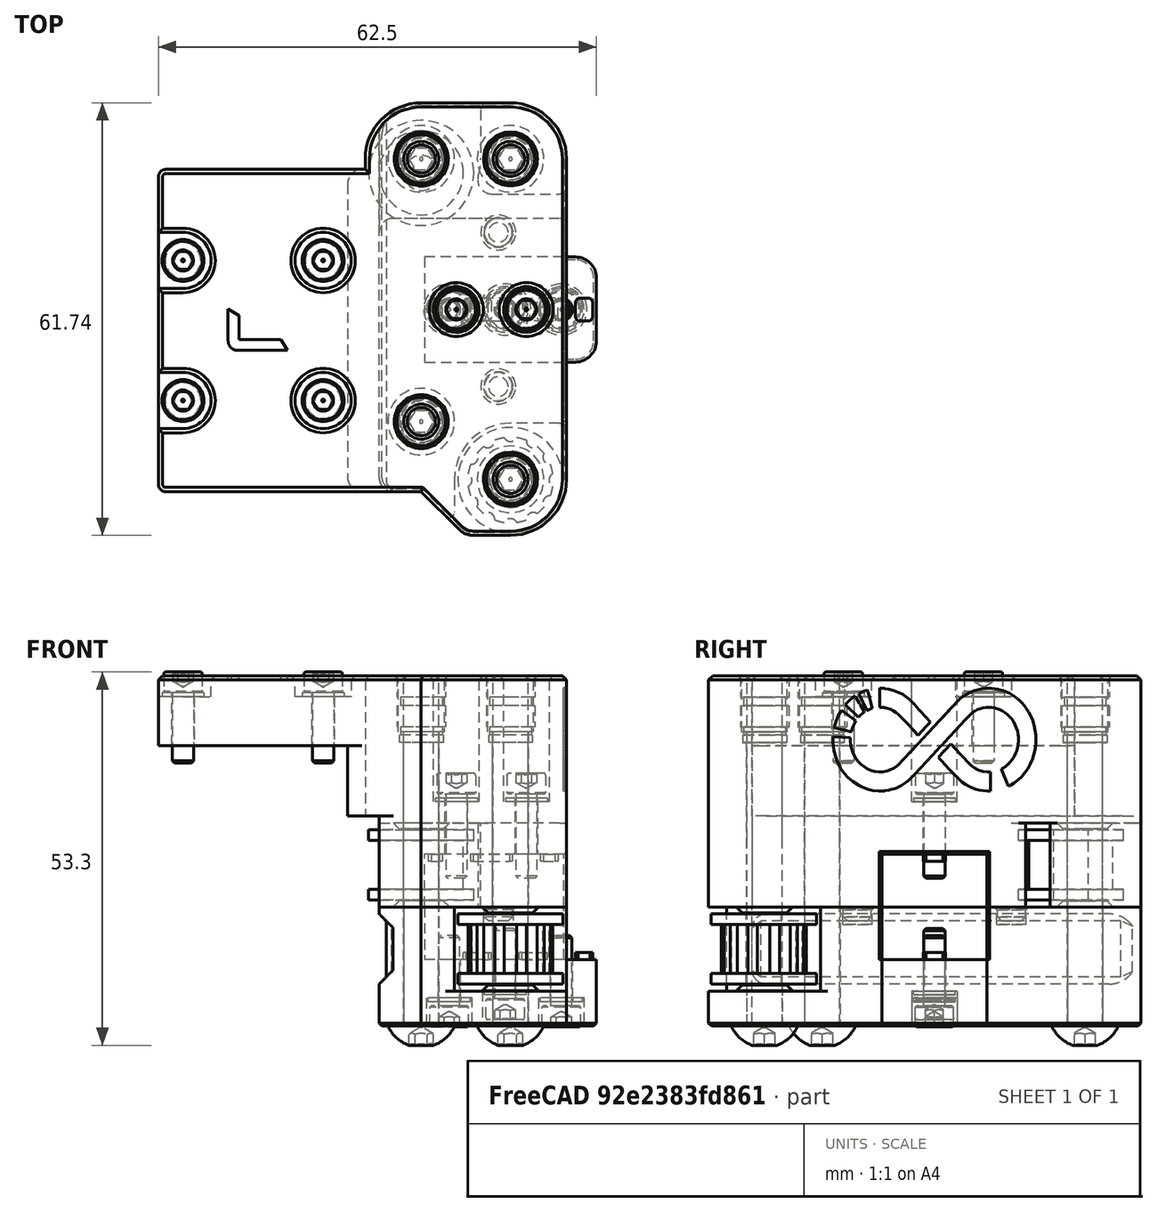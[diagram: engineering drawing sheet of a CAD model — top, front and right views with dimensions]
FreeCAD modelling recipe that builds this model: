
FCSTD DOCUMENT  (FreeCAD 0.19R24291 (Git))
Label: y-carrier-left-1515-assembly
License: Other
LicenseURL: GPL3
objects: Part::FeaturePython×26, Part::Feature×4, Spreadsheet::Sheet×2, PartDesign::CoordinateSystem×1, App::Part×1
note: 31 computed .brp shape members not serialized (recipe doc carries the construction recipe); baked Part::Feature solids carry a one-line shape summary decoded from their .brp

FEATURE [Part::Feature] Cut001002  label="smooth-idler-6mm"
  Placement = pos=(-2,0.5,0) rot=(0,0,1;0rad)
  shape: bbox 15 x 15 x 10 mm, 8 faces (baked)
FEATURE [Part::Feature] Cut002001001  label="20t-idler"
  Placement = pos=(0,-4.61,0) rot=(0,0,1;0rad)
  shape: bbox 15 x 15 x 10 mm, 31 faces (baked)
FEATURE [Part::FeaturePython] Screw003  label="M5x50-Screw"  # Fasteners workbench fastener (typed FeaturePython)
  Placement = pos=(9,-16,3) rot=(1,0,0;3.14159rad)
  diameter = 3
  invert = true
  length = 11
  lengthCustom = 50
  matchOuter = true
  offset = 0
  thread = false
  type = 39
FEATURE [Part::FeaturePython] Screw004  label="M5x50-Screw004"  # Fasteners workbench fastener (typed FeaturePython)
  Placement = pos=(9,21.5,3) rot=(1,0,0;3.14159rad)
  diameter = 3
  invert = true
  length = 11
  lengthCustom = 50
  matchOuter = true
  offset = 0
  thread = false
  type = 39
FEATURE [Part::FeaturePython] Screw005  label="M5x50-Screw005"  # Fasteners workbench fastener (typed FeaturePython)
  Placement = pos=(21.74,21.5,3) rot=(1,0,0;3.14159rad)
  diameter = 3
  invert = true
  length = 11
  lengthCustom = 50
  matchOuter = true
  offset = 0
  thread = false
  type = 39
FEATURE [Part::FeaturePython] Screw006  label="M5x50-Screw003"  # Fasteners workbench fastener (typed FeaturePython)
  Placement = pos=(21.74,-24.24,3) rot=(1,0,0;3.14159rad)
  diameter = 3
  invert = true
  length = 11
  lengthCustom = 50
  matchOuter = true
  offset = 0
  thread = false
  type = 39
FEATURE [Part::FeaturePython] Washer003  label="M3-Washer"  # Fasteners workbench fastener (typed FeaturePython)
  Placement = pos=(-25,-13,50) rot=(0,0,1;0rad)
  diameter = 4
  invert = false
  matchOuter = true
  offset = 0
  type = 5
FEATURE [Part::FeaturePython] Washer004  label="M3-Washer004"  # Fasteners workbench fastener (typed FeaturePython)
  Placement = pos=(-25,7,50) rot=(0,0,1;0rad)
  diameter = 4
  invert = false
  matchOuter = true
  offset = 0
  type = 5
FEATURE [Part::FeaturePython] Washer005  label="M3-Washer005"  # Fasteners workbench fastener (typed FeaturePython)
  Placement = pos=(-5,7,50) rot=(0,0,1;0rad)
  diameter = 4
  invert = false
  matchOuter = true
  offset = 0
  type = 5
FEATURE [Part::FeaturePython] Washer006  label="M3-Washer006"  # Fasteners workbench fastener (typed FeaturePython)
  Placement = pos=(-5,-13,50) rot=(0,0,1;0rad)
  diameter = 4
  invert = false
  matchOuter = true
  offset = 0
  type = 5
FEATURE [Part::FeaturePython] Screw007  label="M3x10-Screw"  # Fasteners workbench fastener (typed FeaturePython)
  Placement = pos=(-25,7,50.55) rot=(0,0,1;0rad)
  baseObject = -> Washer004 [Edge1]
  diameter = 4
  invert = false
  length = 3
  lengthCustom = 10
  matchOuter = true
  offset = 0
  thread = false
  type = 33
FEATURE [Part::FeaturePython] Screw008  label="M3x10-Screw005"  # Fasteners workbench fastener (typed FeaturePython)
  Placement = pos=(-25,-13,50.55) rot=(0,0,1;0rad)
  baseObject = -> Washer003 [Edge1]
  diameter = 4
  invert = false
  length = 3
  lengthCustom = 10
  matchOuter = true
  offset = 0
  thread = false
  type = 33
FEATURE [Part::FeaturePython] Screw009  label="M3x10-Screw004"  # Fasteners workbench fastener (typed FeaturePython)
  Placement = pos=(-5,-13,50.55) rot=(0,0,1;0rad)
  baseObject = -> Washer006 [Edge1]
  diameter = 4
  invert = false
  length = 3
  lengthCustom = 10
  matchOuter = true
  offset = 0
  thread = false
  type = 33
FEATURE [Part::FeaturePython] Screw010  label="M3x10-Screw006"  # Fasteners workbench fastener (typed FeaturePython)
  Placement = pos=(-5,7,50.55) rot=(0,0,1;0rad)
  baseObject = -> Washer005 [Edge1]
  diameter = 4
  invert = false
  length = 3
  lengthCustom = 10
  matchOuter = true
  offset = 0
  thread = false
  type = 33
FEATURE [Part::Feature] Chamfer030007001  label="y-carrier-bottom-left"
  Placement = pos=(0,0,3) rot=(0,0,1;0rad)
  shape: bbox 31 x 61.74 x 17.85 mm, 119 faces (baked)
FEATURE [Part::Feature] Cut002001  label="y-carrier-top-left"
  Placement = pos=(0,0,3) rot=(0,0,1;0rad)
  shape: bbox 58.24 x 61.74 x 35 mm, 468 faces (baked)
FEATURE [Part::FeaturePython] Washer  label="M3-Washer007"  # Fasteners workbench fastener (typed FeaturePython)
  Placement = pos=(13,0,7) rot=(1,0,0;3.14159rad)
  baseObject = -> Chamfer030007001 [Edge6]
  diameter = 4
  invert = false
  matchOuter = true
  offset = 0
  type = 5
FEATURE [Part::FeaturePython] Washer007  label="M3-Washer009"  # Fasteners workbench fastener (typed FeaturePython)
  Placement = pos=(21,0,8) rot=(1,0,0;3.14159rad)
  baseObject = -> Chamfer030007001 [Edge219]
  diameter = 4
  invert = false
  matchOuter = true
  offset = 0
  type = 5
FEATURE [Part::FeaturePython] Washer008  label="M3-Washer008"  # Fasteners workbench fastener (typed FeaturePython)
  Placement = pos=(29,0,7) rot=(1,0,0;3.14159rad)
  baseObject = -> Chamfer030007001 [Edge217]
  diameter = 4
  invert = false
  matchOuter = true
  offset = 0
  type = 5
FEATURE [Part::FeaturePython] Screw  label="M3x10-Screw010"  # Fasteners workbench fastener (typed FeaturePython)
  Placement = pos=(13,0,5.9) rot=(1,0,0;3.14159rad)
  diameter = 4
  invert = false
  length = 3
  lengthCustom = 10
  matchOuter = true
  offset = 0
  thread = false
  type = 33
FEATURE [Part::FeaturePython] Screw011  label="M3x10-Screw011"  # Fasteners workbench fastener (typed FeaturePython)
  Placement = pos=(21,0,6.9) rot=(1,0,0;3.14159rad)
  diameter = 4
  invert = false
  length = 3
  lengthCustom = 10
  matchOuter = true
  offset = 0
  thread = false
  type = 33
FEATURE [Part::FeaturePython] Screw012  label="M3x10-Screw012"  # Fasteners workbench fastener (typed FeaturePython)
  Placement = pos=(29,0,5.9) rot=(1,0,0;3.14159rad)
  diameter = 4
  invert = false
  length = 3
  lengthCustom = 10
  matchOuter = true
  offset = 0
  thread = false
  type = 33
FEATURE [Part::FeaturePython] Washer012  label="M3-Washer013"  # Fasteners workbench fastener (typed FeaturePython)
  Placement = pos=(14,0,35) rot=(0,0,1;0rad)
  baseObject = -> Cut002001 [Edge1110]
  diameter = 4
  invert = false
  matchOuter = true
  offset = 0
  type = 5
FEATURE [Part::FeaturePython] Washer013  label="M3-Washer014"  # Fasteners workbench fastener (typed FeaturePython)
  Placement = pos=(24,0,35) rot=(0,0,1;0rad)
  baseObject = -> Cut002001 [Edge1112]
  diameter = 4
  invert = false
  matchOuter = true
  offset = 0
  type = 5
FEATURE [Part::FeaturePython] Screw013  label="M3x12-Screw"  # Fasteners workbench fastener (typed FeaturePython)
  Placement = pos=(14,0,36.1) rot=(0,0,1;0rad)
  diameter = 4
  invert = false
  length = 4
  lengthCustom = 12
  matchOuter = true
  offset = 0
  thread = false
  type = 33
FEATURE [Part::FeaturePython] Screw014  label="M3x12-Screw001"  # Fasteners workbench fastener (typed FeaturePython)
  Placement = pos=(24,0,36.1) rot=(0,0,1;0rad)
  diameter = 4
  invert = false
  length = 4
  lengthCustom = 12
  matchOuter = true
  offset = 0
  thread = false
  type = 33
FEATURE [Part::FeaturePython] HeatSet  label="M5-HeatSet"  # WARN: FeaturePython — macro-defined, semantics opaque (R4)
  Placement = pos=(9,-16,53) rot=(0,0,1;0rad)
  baseObject = -> Cut002001 [Edge926]
  diameter = 5
  invert = false
  offset = 0
FEATURE [Part::FeaturePython] HeatSet001  label="M5-HeatSet001"  # WARN: FeaturePython — macro-defined, semantics opaque (R4)
  Placement = pos=(21.74,-24.24,53) rot=(0,0,1;0rad)
  baseObject = -> Cut002001 [Edge927]
  diameter = 5
  invert = false
  offset = 0
FEATURE [Part::FeaturePython] HeatSet002  label="M5-HeatSet002"  # WARN: FeaturePython — macro-defined, semantics opaque (R4)
  Placement = pos=(9,21.5,53) rot=(0,0,1;0rad)
  baseObject = -> Cut002001 [Edge931]
  diameter = 5
  invert = false
  offset = 0
FEATURE [Part::FeaturePython] HeatSet003  label="M5-HeatSet003"  # WARN: FeaturePython — macro-defined, semantics opaque (R4)
  Placement = pos=(21.74,21.5,53) rot=(0,0,1;0rad)
  baseObject = -> Cut002001 [Edge932]
  diameter = 5
  invert = false
  offset = 0
FEATURE [PartDesign::CoordinateSystem] LCS_Y_carrier_left  label="LCS_Y-carrier-left"
  AttacherType = Attacher::AttachEngine3D
FEATURE [App::Part] Part  label="Y-carrier-left"
  Group = -> [Cut001002,Cut002001001,Washer003,Washer004,Washer005,Screw007,Washer006,Screw009,Screw008,Screw010,Screw006,Screw004,Screw005,Screw003,Cut002001,Chamfer030007001,Washer007,Screw012,Screw011,Screw,Washer008,Washer,Washer013,Screw014,Screw013,Washer012,HeatSet003,HeatSet,HeatSet001,HeatSet002,LCS_Y_carrier_left]
  Origin = -> Origin
FEATURE [Spreadsheet::Sheet] Fasteners_BOM
  cells = A1=Type; B1=Qty; A2=Heat Set Insert M5; B2=8; A3=ISO4762 Screw M3x10; B3=14; A4=ISO4762 Screw M3x12; B4=4; A5=ISO7092 Washer M3; B5=26; A6=ISO7380-1 Screw M5x50; B6=8
FEATURE [Spreadsheet::Sheet] Fasteners_BOM001
  cells = A1=Type; B1=Qty; A2=Heat Set Insert M5; B2=8; A3=ISO4762 Screw M3x10; B3=14; A4=ISO4762 Screw M3x12; B4=4; A5=ISO7092 Washer M3; B5=26; A6=ISO7380-1 Screw M5x50; B6=8
